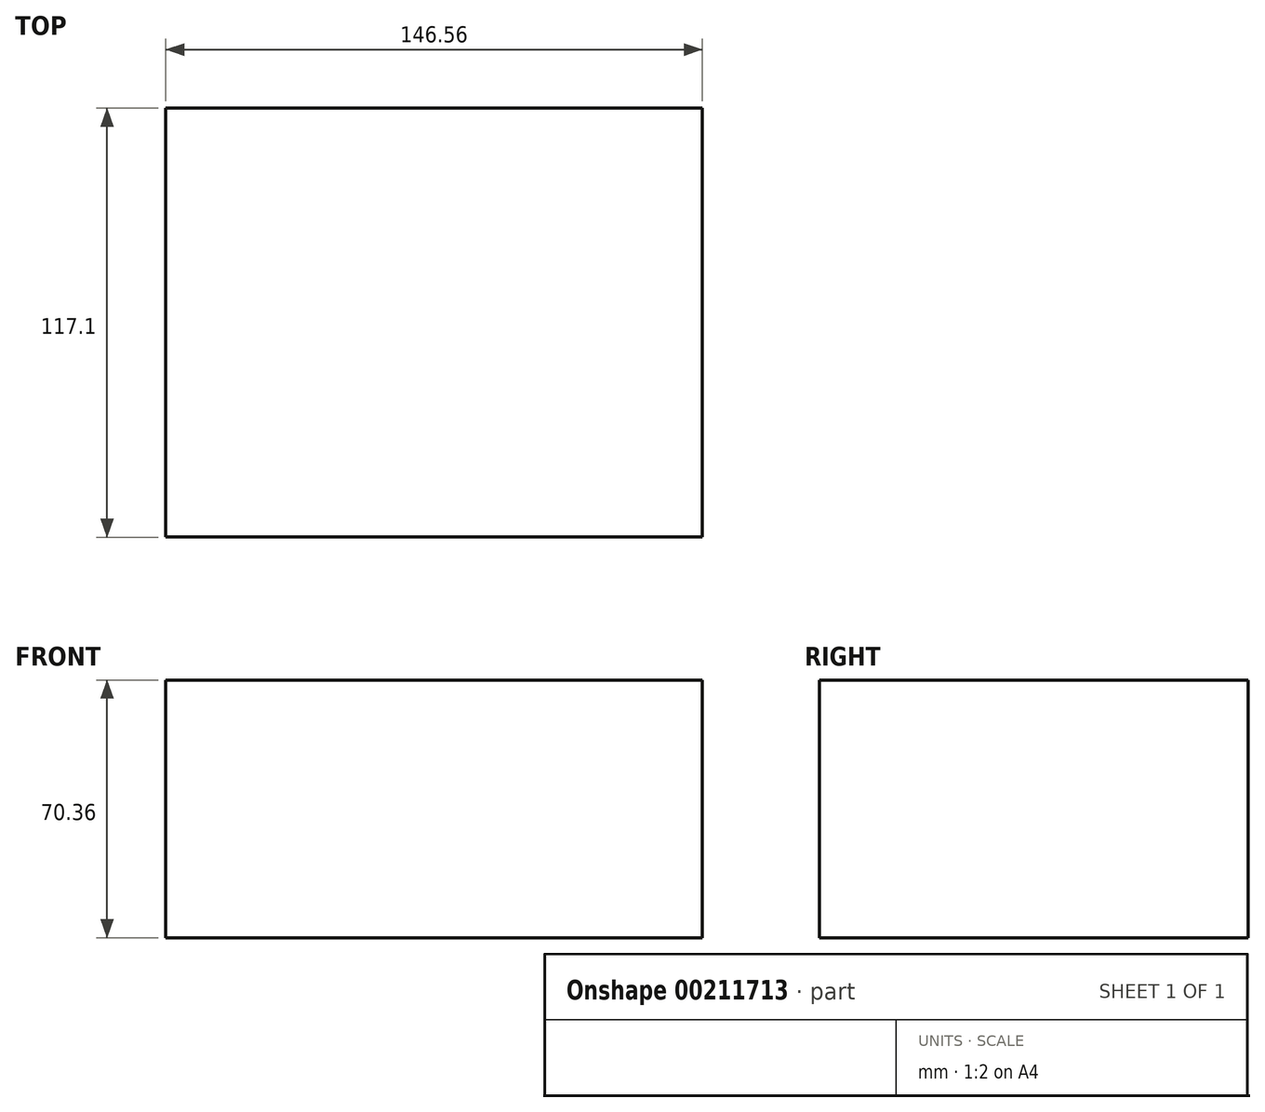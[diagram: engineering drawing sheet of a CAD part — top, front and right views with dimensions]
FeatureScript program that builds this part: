
annotation { "Feature Type Name" : "Feature", "Feature Type Description" : "" }
export const myFeature = defineFeature(function(context is Context, id is Id, definition is map)
    precondition{}
    {
        {
            var Q0;
            Q0=qCreatedBy(makeId("Top.planeOp"),FACE);
            var sketch = newSketch(context, id + "F0", { "sketchPlane" : qUnion([Q0])});
            skLineSegment(sketch, "E0.bottom", {"start": v(73.28, 58.55) * mm, "end": v(-73.28, 58.55) * mm});
            skLineSegment(sketch, "E0.top", {"start": v(73.28, -58.55) * mm, "end": v(-73.28, -58.55) * mm});
            skLineSegment(sketch, "E0.left", {"start": v(73.28, 58.55) * mm, "end": v(73.28, -58.55) * mm});
            skLineSegment(sketch, "E0.right", {"start": v(-73.28, 58.55) * mm, "end": v(-73.28, -58.55) * mm});
            skPoint(sketch, "E0.middle", {"position": v(0, 0) * mm});
            skSolve(sketch);
        }
        {
            var Q0;
            Q0=qCreatedBy(makeId("Front.planeOp"),FACE);
            var sketch = newSketch(context, id + "F1", { "sketchPlane" : qUnion([Q0])});
            skLineSegment(sketch, "E1", {"start": v(0, 0) * mm, "end": v(0, 70.36) * mm});
            skSolve(sketch);
        }
        {
            var Q0;
            Q0=makeQuery(id+"F0.imprint","IMPRINT",FACE,{"disambiguationData":[TD([[makeQuery(id+"F0.imprint","IMPRINT",EDGE,{"derivedFrom":sQuery(id+"F0.wireOp",EDGE,"E0.bottom")}),1.0]])]});
            var Q1;
            Q1=sQuery(id+"F1.wireOp",EDGE,"E1");
            sweep(context, id + "F2", {"profiles" : qUnion([Q0]), "path" : qUnion([Q1])});
        }
    });
